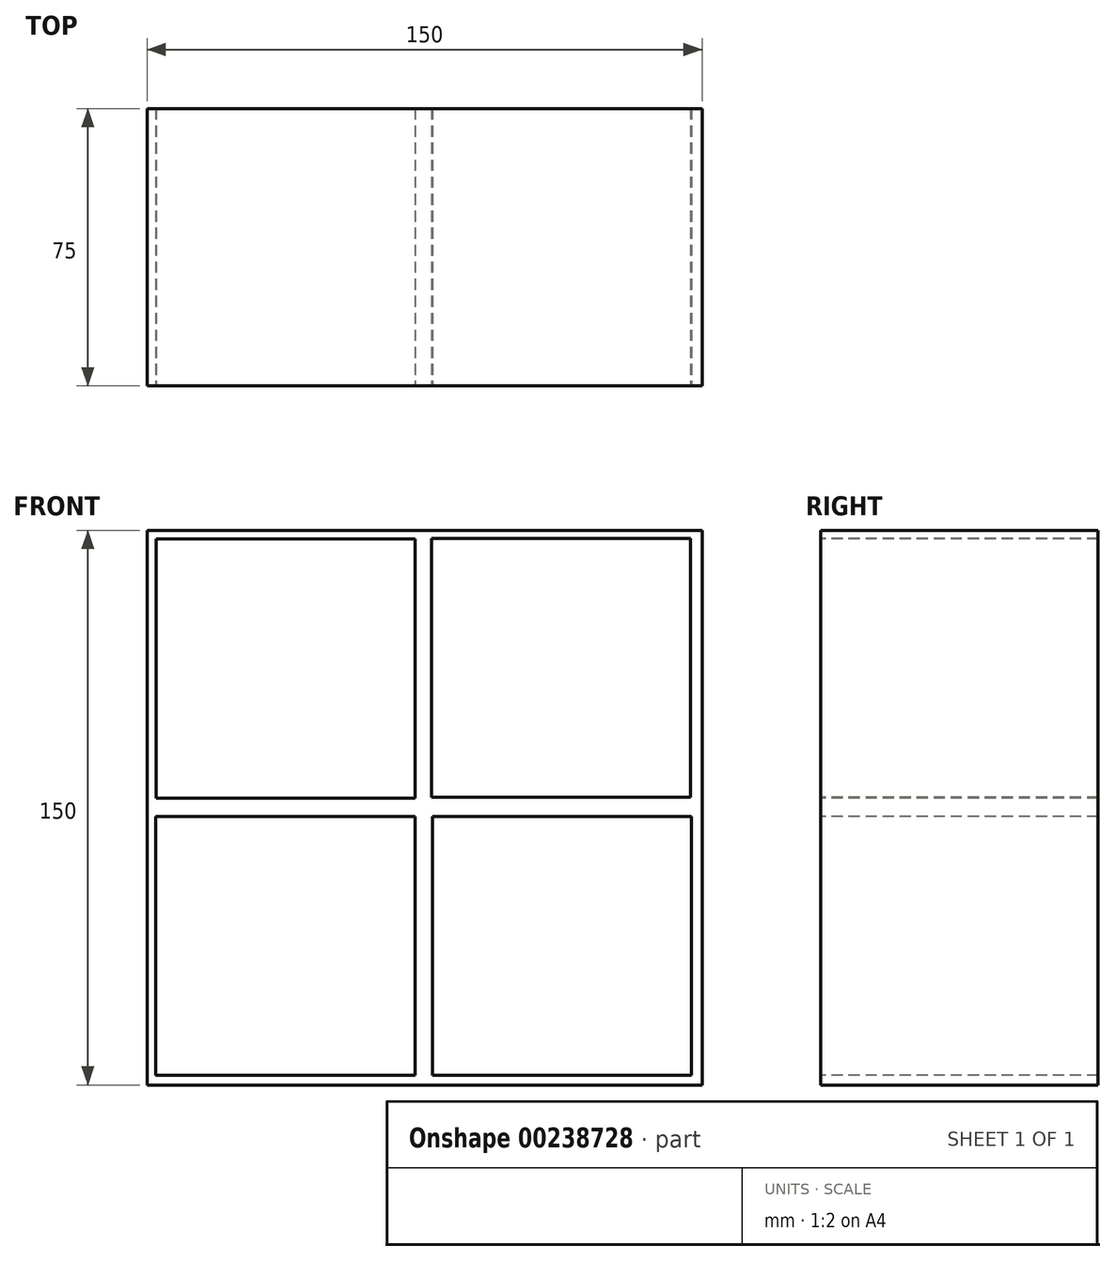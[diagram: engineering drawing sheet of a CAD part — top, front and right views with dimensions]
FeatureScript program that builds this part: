
annotation { "Feature Type Name" : "Feature", "Feature Type Description" : "" }
export const myFeature = defineFeature(function(context is Context, id is Id, definition is map)
    precondition{}
    {
        {
            var Q0;
            Q0=qCreatedBy(makeId("Top.planeOp"),FACE);
            var sketch = newSketch(context, id + "F0", { "sketchPlane" : qUnion([Q0])});
            skLineSegment(sketch, "E0.bottom", {"start": v(-74.96, -5.21) * mm, "end": v(75.04, -5.21) * mm});
            skLineSegment(sketch, "E0.top", {"start": v(-74.96, 69.79) * mm, "end": v(75.04, 69.79) * mm});
            skLineSegment(sketch, "E0.left", {"start": v(-74.96, -5.21) * mm, "end": v(-74.96, 69.79) * mm});
            skLineSegment(sketch, "E0.right", {"start": v(75.04, -5.21) * mm, "end": v(75.04, 69.79) * mm});
            skSolve(sketch);
        }
        {
            var Q0;
            Q0 = qSketchRegion(id + "F0", true);
            extrude(context, id + "F1", {"entities" : qUnion([Q0]), "depth" : 150 * mm});
        }
        {
            var Q0;
            Q0=makeQuery(id+"F1.opExtrude","SWEPT_FACE",FACE,{"disambiguationData":[OSD([sQuery(id+"F0.wireOp",EDGE,"E0.bottom")])]});
            var sketch = newSketch(context, id + "F2", { "sketchPlane" : qUnion([Q0])});
            skLineSegment(sketch, "E1", {"start": v(0, 150) * mm, "end": v(0, 0) * mm});
            skLineSegment(sketch, "E2", {"start": v(-74.96, 75) * mm, "end": v(75.04, 75) * mm});
            skLineSegment(sketch, "E3.bottom", {"start": v(-72.51, 147.6) * mm, "end": v(-2.51, 147.6) * mm});
            skLineSegment(sketch, "E3.top", {"start": v(-72.51, 77.6) * mm, "end": v(-2.51, 77.6) * mm});
            skLineSegment(sketch, "E3.left", {"start": v(-72.51, 147.6) * mm, "end": v(-72.51, 77.6) * mm});
            skLineSegment(sketch, "E3.right", {"start": v(-2.51, 147.6) * mm, "end": v(-2.51, 77.6) * mm});
            skLineSegment(sketch, "E4.bottom", {"start": v(1.93, 147.8) * mm, "end": v(71.93, 147.8) * mm});
            skLineSegment(sketch, "E4.top", {"start": v(1.93, 77.8) * mm, "end": v(71.93, 77.8) * mm});
            skLineSegment(sketch, "E4.left", {"start": v(1.93, 147.8) * mm, "end": v(1.93, 77.8) * mm});
            skLineSegment(sketch, "E4.right", {"start": v(71.93, 147.8) * mm, "end": v(71.93, 77.8) * mm});
            skLineSegment(sketch, "E5.bottom", {"start": v(-72.56, 72.6) * mm, "end": v(-2.56, 72.6) * mm});
            skLineSegment(sketch, "E5.top", {"start": v(-72.56, 2.6) * mm, "end": v(-2.56, 2.6) * mm});
            skLineSegment(sketch, "E5.left", {"start": v(-72.56, 72.6) * mm, "end": v(-72.56, 2.6) * mm});
            skLineSegment(sketch, "E5.right", {"start": v(-2.56, 72.6) * mm, "end": v(-2.56, 2.6) * mm});
            skLineSegment(sketch, "E6.bottom", {"start": v(2.12, 72.58) * mm, "end": v(72.12, 72.58) * mm});
            skLineSegment(sketch, "E6.top", {"start": v(2.12, 2.58) * mm, "end": v(72.12, 2.58) * mm});
            skLineSegment(sketch, "E6.left", {"start": v(2.12, 72.58) * mm, "end": v(2.12, 2.58) * mm});
            skLineSegment(sketch, "E6.right", {"start": v(72.12, 72.58) * mm, "end": v(72.12, 2.58) * mm});
            skSolve(sketch);
        }
        {
            var Q0;
            Q0 = qSketchRegion(id + "F2", true);
            extrude(context, id + "F3", {"entities" : qUnion([Q0]), "operationType" : NewBodyOperationType.REMOVE, "oppositeDirection" : true, "depth" : 128.9 * mm});
        }
    });
